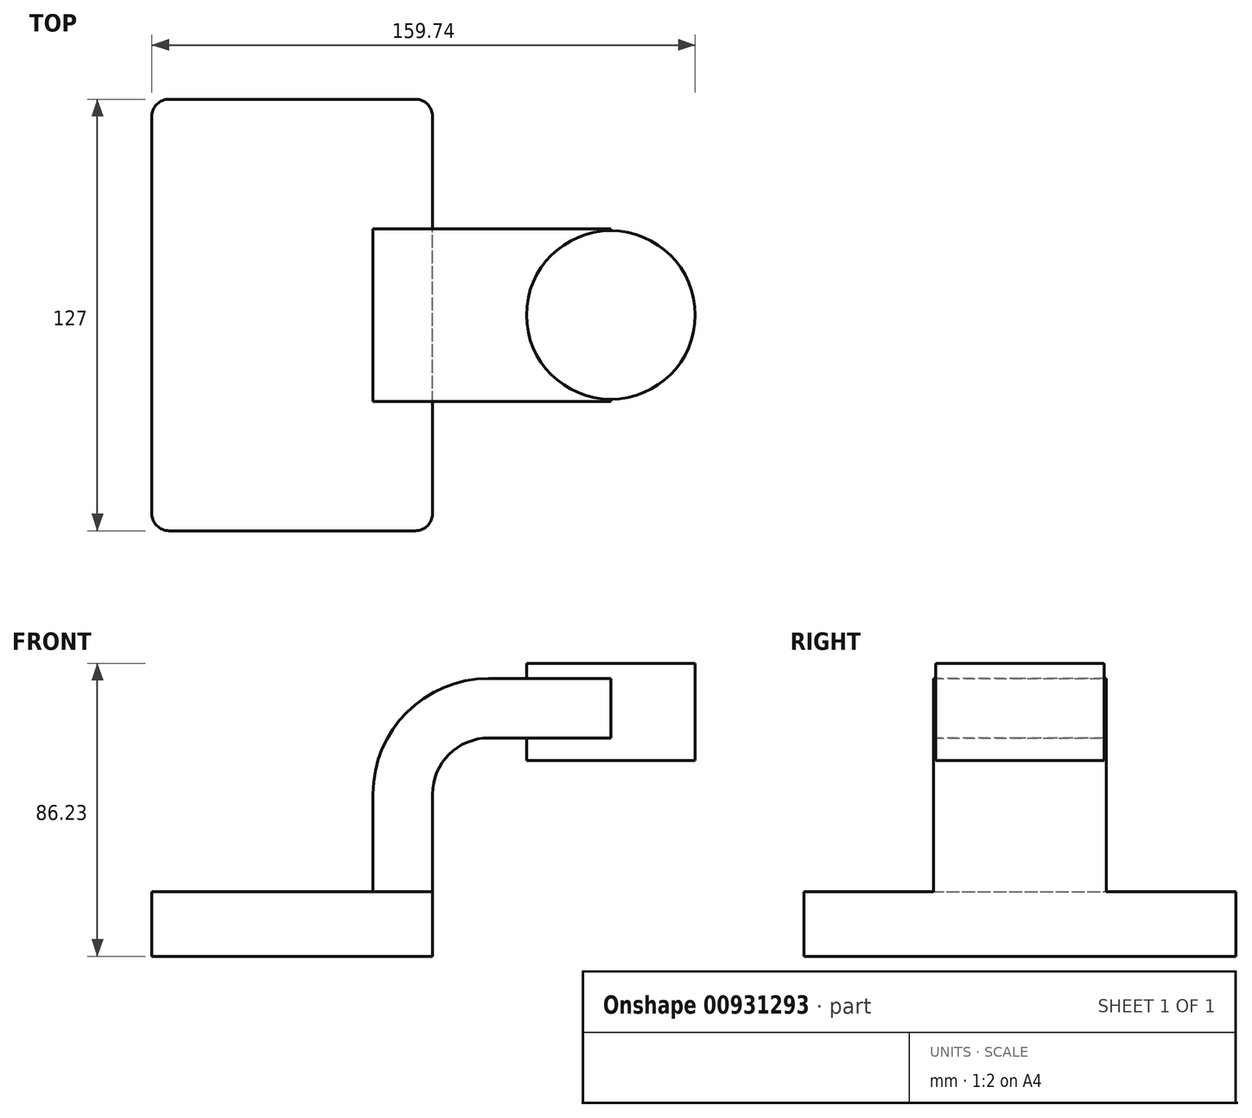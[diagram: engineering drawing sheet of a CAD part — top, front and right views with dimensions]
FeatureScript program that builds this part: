
annotation { "Feature Type Name" : "Feature", "Feature Type Description" : "" }
export const myFeature = defineFeature(function(context is Context, id is Id, definition is map)
    precondition{}
    {
        {
            var Q0;
            Q0=qCreatedBy(makeId("Front.planeOp"),FACE);
            var sketch = newSketch(context, id + "F0", { "sketchPlane" : qUnion([Q0])});
            skLineSegment(sketch, "E0.bottom", {"start": v(-41.28, 9.52) * mm, "end": v(41.28, 9.53) * mm});
            skLineSegment(sketch, "E0.top", {"start": v(-41.28, -9.53) * mm, "end": v(41.28, -9.53) * mm});
            skLineSegment(sketch, "E0.left", {"start": v(-41.28, 9.52) * mm, "end": v(-41.28, -9.53) * mm});
            skLineSegment(sketch, "E0.right", {"start": v(41.28, 9.53) * mm, "end": v(41.28, -9.52) * mm});
            skPoint(sketch, "E0.middle", {"position": v(0, 0) * mm});
            skLineSegment(sketch, "E1.bottom", {"start": v(118.47, 48.13) * mm, "end": v(67.67, 48.13) * mm});
            skLineSegment(sketch, "E1.top", {"start": v(118.47, 76.7) * mm, "end": v(67.67, 76.7) * mm});
            skLineSegment(sketch, "E1.left", {"start": v(118.47, 48.13) * mm, "end": v(118.47, 76.7) * mm});
            skLineSegment(sketch, "E1.right", {"start": v(67.67, 48.13) * mm, "end": v(67.67, 76.7) * mm});
            skPoint(sketch, "E1.middle", {"position": v(93.07, 62.42) * mm});
            skLineSegment(sketch, "E2", {"start": v(41.27, 9.53) * mm, "end": v(41.27, 38.2) * mm});
            skArc(sketch, "E3", {"start": v(41.27, 38.2) * mm, "mid": v(46.11, 49.87) * mm, "end": v(57.78, 54.7) * mm});
            skLineSegment(sketch, "E4", {"start": v(57.78, 54.7) * mm, "end": v(93.68, 54.7) * mm});
            skLineSegment(sketch, "E5.0", {"start": v(57.78, 72.23) * mm, "end": v(93.68, 72.23) * mm});
            skArc(sketch, "E5.1", {"start": v(23.75, 38.2) * mm, "mid": v(33.72, 62.26) * mm, "end": v(57.78, 72.23) * mm});
            skLineSegment(sketch, "E5.2", {"start": v(23.75, 9.53) * mm, "end": v(23.75, 38.2) * mm});
            skLineSegment(sketch, "E6", {"start": v(93.68, 48.13) * mm, "end": v(93.68, 76.7) * mm});
            skFitSpline(sketch, "E7", {"points": [v(-41.28, 9.52) * mm, v(62.78, 72.23) * mm], "startDerivative": vector(17.44, 181.22) * mm, "endDerivative": vector(143.76, -4.77) * mm});
            skSolve(sketch);
        }
        {
            var Q0;
            Q0=makeQuery(id+"F0.imprint","IMPRINT",FACE,{"disambiguationData":[TD([[makeQuery(id+"F0.imprint","IMPRINT",EDGE,{"derivedFrom":sQuery(id+"F0.wireOp",EDGE,"E0.top")}),1.0]])]});
            extrude(context, id + "F1", {"entities" : qUnion([Q0]), "endBound" : BoundingType.SYMMETRIC, "depth" : 127 * mm, "offsetDistance" : 25.4 * mm});
        }
        {
            var Q0;
            {var subQ1=sQuery(id+"F0.wireOp",EDGE,"E2");Q0=makeQuery(id+"F0.imprint","IMPRINT",FACE,{"disambiguationData":[TD([[makeQuery(id+"F0.imprint","IMPRINT",EDGE,{"derivedFrom":subQ1}),1.0]])]});}
            var Q1;
            {var subQ0=sQuery(id+"F0.wireOp",EDGE,"E4");var subQ1=sQuery(id+"F0.wireOp",EDGE,"E1.right");var subQ2=makeQuery(id+"F0.imprint","INTERSECT",VERTEX,{"derivedFrom":[subQ1,subQ0]});Q1=makeQuery(id+"F0.imprint","IMPRINT",FACE,{"disambiguationData":[TD([[makeQuery(id+"F0.imprint","IMPRINT",EDGE,{"disambiguationData":[TD([[subQ2,-1.0]])],"derivedFrom":subQ1}),-1.0]])]});}
            extrude(context, id + "F2", {"entities" : qUnion([Q0, Q1]), "operationType" : NewBodyOperationType.ADD, "endBound" : BoundingType.SYMMETRIC, "depth" : 50.8 * mm, "offsetDistance" : 25.4 * mm});
        }
        {
            var Q0;
            {var subQ1=sQuery(id+"F0.wireOp",EDGE,"E5.1");Q0=makeQuery(id+"F0.imprint","IMPRINT",FACE,{"disambiguationData":[TD([[makeQuery(id+"F0.imprint","IMPRINT",EDGE,{"derivedFrom":subQ1}),1.0]])]});}
            extrude(context, id + "F3", {"entities" : qUnion([Q0]), "operationType" : NewBodyOperationType.ADD, "endBound" : BoundingType.SYMMETRIC, "depth" : 15.88 * mm, "offsetDistance" : 25.4 * mm});
        }
        {
            var Q0;
            {var subQ0=sQuery(id+"F0.wireOp",EDGE,"E1.left");Q0=makeQuery(id+"F0.imprint","IMPRINT",FACE,{"disambiguationData":[TD([[makeQuery(id+"F0.imprint","IMPRINT",EDGE,{"derivedFrom":subQ0}),1.0]])]});}
            var Q1;
            Q1=sQuery(id+"F0.wireOp",EDGE,"E6");
            revolve(context, id + "F4", {"operationType" : NewBodyOperationType.ADD, "surfaceOperationType" : NewSurfaceOperationType.NEW, "entities" : qUnion([Q0]), "axis" : qUnion([Q1]), "revolveType" : RevolveType.FULL});
        }
        {
            var Q0;
            Q0=makeQuery(id+"F1.opExtrude","CAP_EDGE",EDGE,{"disambiguationData":[OSD([sQuery(id+"F0.wireOp",EDGE,"E0.right")])],"isStart":true});
            var Q1;
            Q1=makeQuery(id+"F1.opExtrude","CAP_EDGE",EDGE,{"disambiguationData":[OSD([sQuery(id+"F0.wireOp",EDGE,"E0.left")])],"isStart":true});
            var Q2;
            Q2=makeQuery(id+"F1.opExtrude","CAP_EDGE",EDGE,{"disambiguationData":[OSD([sQuery(id+"F0.wireOp",EDGE,"E0.left")])],"isStart":false});
            var Q3;
            Q3=makeQuery(id+"F1.opExtrude","CAP_EDGE",EDGE,{"disambiguationData":[OSD([sQuery(id+"F0.wireOp",EDGE,"E0.right")])],"isStart":false});
            fillet(context, id + "F5", {"entities" : qUnion([Q0, Q1, Q2, Q3]), "radius" : 5.08 * mm, "tangentPropagation" : true, "allowEdgeOverflow" : false});
        }
    });
